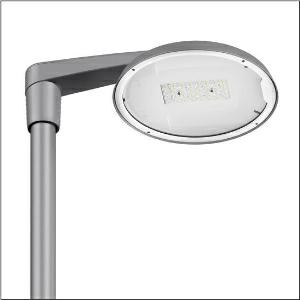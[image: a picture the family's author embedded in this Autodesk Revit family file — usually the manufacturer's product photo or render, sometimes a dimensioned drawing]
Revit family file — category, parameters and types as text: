
# Revit family: dl_r__50_iq_mini___st0_5a_5xa248b31f08he_0d04
name_source: partatom
category: Lighting Fixtures
units: mm (PartAtom-declared; Revit-internal decimal feet)

## family parameters
Cut with Voids When Loaded = No
Host = Face
Light Source = No
Part Type = Normal
Room Calculation Point = No
Round Connector Dimension = Use Diameter
Shared = No

## types (1)
- --- (1 x LED, 9400 lm, 68.6 W, 3000K)
    Apparent Load = 69 VA
    CIE Flux Codes = 41 75 97 100 100
    Color Rendering = 70
    Color Temperature = 3000K
    Default Elevation = 1800 mm
    Description = DL® 50 iQ mini, mast luminaire, primary light control with lens, of PMMA, primary optical cover: cover, of toughened safety glass, transparent, light distribution: ST0.5a, light emission: direct distribution, primary light characteristic: asymmetric, installation type: side-entry, post-top, LED, High Power LED, rated luminous flux: 9.400lm, luminous efficacy: 137lm/W, light colour: 730, colour temperature: 3000K, control: optimised constant luminous flux control (CLO 2.0), Desk-Remote (wireless, voltage-free reading and setting of iQ features in the workshop via application-optimized NFC function/RFID function), Light-Fading, Smart-Wire, Night-Set, Lumen-Switch, Temp-Guard, Auto-Match, Street-Remote, mains connection: 230..240V, AC, 50/60Hz, connection cable pre-assembled, cable length: 8,5m, start of lifetime: 69W, end of service life: 72W, reduction: 30W, luminaire housing, of diecast aluminium, powder-coated, Siteco® metallic grey (DB 702S), inclination adjustable: 0°, 5°, 10° (post-top) | 0°, -5°, -10°, -15° (side-entry), please order mast post-top element or mast side-entry element separately, diameter: 500mm, height: 115mm, post-top: for spigot size d x l = 76 x 100mm; with reducer (optional accessory) 60 x 100mm | side-entry: for spigot size d x l = 60 x 100mm; with reducer (optional accessory) 42 x 100mm, protection rating (complete): IP66, insulation class (complete): insulation class II (safety insulation), certification: CE, ENEC, VDE, impact resistance: IK08, permissible operating ambient temperature for outdoor applications: -25..+40°C, standard-compliant lighting for roads and squares, packaging unit: 1 piece

Light Distribution: ST0.5a
    Height = 115 mm
    Lamp = 1 x LED
    Lamp Light Flux = 9400 lm
    Lamp Power = 68.6 W
    Lamp count = 1
    Length = 500 mm
    Luminous efficacy = 137 lm/W
    Manufacturer = Siteco
    ModVariant = No
    Model = 5XA248B31F08HE
    Number of Poles = 1
    OnlyDefault = Yes
    Power Factor = 1
    Product Name = DL® 50 iQ mini | ST0.5a
    Product group = mast luminaire | pylon top
    ProductGroupID = 6100
    Protection Class = Protection class II
    Protection Degree = IP 66
    RLX_Detail_Level = 1
    RLX_Emergency_Light_Flux = 0 lm
    RLX_Emergency_Type = 0
    RLX_Emergency_Type_DB = No
    RlxData = <blob elided: 126769 chars, md5=e3d96181>
    Socket = socket
    Standby Power = 0 W
    System Light Flux = 9400 lm
    System Power = 69 W
    Type Comments = factory setting: luminous flux: 100 % | dim-lin: 254 | 693 mA
    Type Image = l_1251794.jpg
    URL = http://relux.com
    VarID = @adj_092593
    Voltage = 0 V
    Weight = 0.00 kg
    Width = 0 mm  [stored 0 ft]

note: [stored X ft] marks values corroborated as IEEE doubles in the binary element streams (Revit-internal decimal feet)

## geometry (parser evidence)
native form markers: Blend x4, Sweep x10
no freeform markers — native parametric forms only
